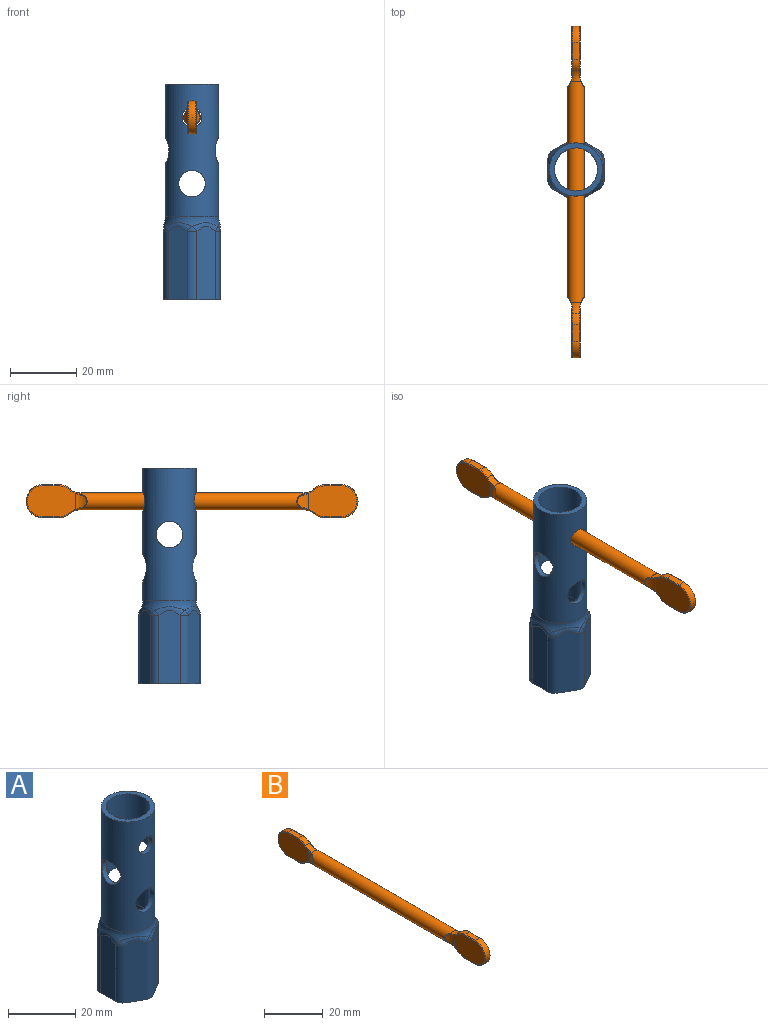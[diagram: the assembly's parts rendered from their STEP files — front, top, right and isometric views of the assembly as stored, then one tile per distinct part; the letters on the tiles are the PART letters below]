
ASSEMBLY  parts=2 mates=1
PART A: 60 faces, bbox 20.5x20.5x65 mm
  f0: cylinder r=8mm len=40mm, axis (0,0,-1), area 1745mm2, adj f9,f10,f54,f55,f56,f57,f58,f59
  f1: cylinder r=6.5mm len=40mm, axis (0,0,-1), area 1363.3mm2, adj f10,f35,f54,f55,f56,f57,f58,f59
  f2: plane 22.22x5.5mm, normal (0.5,0.87,0), area 137mm2, adj f8,f11,f16,f20
  f3: plane 22.22x5.5mm, normal (-0.5,0.87,0), area 137mm2, adj f8,f11,f12,f24
  f4: plane 22.22x6.35mm, normal (-1,0,0), area 137mm2, adj f8,f12,f13,f28
  f5: plane 22.22x5.5mm, normal (-0.5,-0.87,0), area 137mm2, adj f8,f13,f14,f25
  f6: plane 22.22x5.5mm, normal (0.5,-0.87,0), area 137mm2, adj f8,f14,f15,f21
  f7: plane 22.22x6.35mm, normal (1,0,0), area 137mm2, adj f8,f15,f16,f17
  f8: plane 18.7x17mm, normal (0,0,-1), area 78.4mm2, adj f2,f3,f4,f5,f6,f7,f11,f12
  f9: torus R=13mm, axis (0,0,1), area 112.2mm2, adj f0,f17,f20,f21,f24,f25,f28
  f10: plane 16x16mm, normal (0,0,1), area 68.3mm2, adj f0,f1
  f11: cylinder r=3mm len=20.55mm, axis (0,0,-1), area 64.6mm2, adj f2,f3,f8,f22
  f12: cylinder r=3mm len=20.55mm, axis (0,0,-1), area 64.6mm2, adj f3,f4,f8,f26
  f13: cylinder r=3mm len=20.55mm, axis (0,0,-1), area 64.6mm2, adj f4,f5,f8,f27
  f14: cylinder r=3mm len=20.55mm, axis (0,0,-1), area 64.6mm2, adj f5,f6,f8,f23
  f15: cylinder r=3mm len=20.55mm, axis (0,0,-1), area 64.6mm2, adj f6,f7,f8,f19
  f16: cylinder r=3mm len=20.55mm, axis (0,0,-1), area 64.6mm2, adj f2,f7,f8,f18
  f17: bspline ~10.91x3.77mm, area 12.7mm2, adj f7,f9,f18,f19
  f18: sphere r=3mm, area 2.9mm2, adj f16,f17,f20
  f19: sphere r=3mm, area 2.9mm2, adj f15,f17,f21
  f20: bspline ~9.65x6.03mm, area 12.7mm2, adj f2,f9,f18,f22
  f21: bspline ~9.49x6.34mm, area 12.7mm2, adj f6,f9,f19,f23
  f22: sphere r=3mm, area 2.9mm2, adj f11,f20,f24
  f23: sphere r=3mm, area 2.9mm2, adj f14,f21,f25
  f24: bspline ~9.49x6.34mm, area 12.7mm2, adj f3,f9,f22,f26
  f25: bspline ~9.65x6.03mm, area 12.7mm2, adj f5,f9,f23,f27
  f26: sphere r=3mm, area 2.9mm2, adj f12,f24,f28
  f27: sphere r=3mm, area 2.9mm2, adj f13,f25,f28
  f28: bspline ~10.91x3.77mm, area 12.7mm2, adj f4,f9,f26,f27
  f29: plane 22.22x5.5mm, normal (-0.5,-0.87,0), area 137mm2, adj f8,f36,f41,f45
  f30: plane 22.22x5.5mm, normal (0.5,-0.87,0), area 137mm2, adj f8,f36,f37,f49
  f31: plane 22.22x6.35mm, normal (1,0,0), area 137mm2, adj f8,f37,f38,f53
  f32: plane 22.22x5.5mm, normal (0.5,0.87,0), area 137mm2, adj f8,f38,f39,f50
  f33: plane 22.22x5.5mm, normal (-0.5,0.87,0), area 137mm2, adj f8,f39,f40,f46
  f34: plane 22.22x6.35mm, normal (-1,0,0), area 137mm2, adj f8,f40,f41,f42
  f35: torus R=13mm, axis (0,0,1), area 120mm2, adj f1,f42,f45,f46,f49,f50,f53
  f36: cylinder r=1.5mm len=20.55mm, axis (0,0,-1), area 32.3mm2, adj f8,f29,f30,f47
  f37: cylinder r=1.5mm len=20.55mm, axis (0,0,-1), area 32.3mm2, adj f8,f30,f31,f51
  f38: cylinder r=1.5mm len=20.55mm, axis (0,0,-1), area 32.3mm2, adj f8,f31,f32,f52
  f39: cylinder r=1.5mm len=20.55mm, axis (0,0,-1), area 32.3mm2, adj f8,f32,f33,f48
  f40: cylinder r=1.5mm len=20.55mm, axis (0,0,-1), area 32.3mm2, adj f8,f33,f34,f44
  f41: cylinder r=1.5mm len=20.55mm, axis (0,0,-1), area 32.3mm2, adj f8,f29,f34,f43
  f42: bspline ~9.54x3.25mm, area 6.1mm2, adj f34,f35,f43,f44
  f43: sphere r=1.5mm, area 0.7mm2, adj f41,f42,f45
  f44: sphere r=1.5mm, area 0.7mm2, adj f40,f42,f46
  f45: bspline ~8.37x5.06mm, area 6.1mm2, adj f29,f35,f43,f47
  f46: bspline ~8.29x5.22mm, area 6.1mm2, adj f33,f35,f44,f48
  f47: sphere r=1.5mm, area 0.7mm2, adj f36,f45,f49
  f48: sphere r=1.5mm, area 0.7mm2, adj f39,f46,f50
  f49: bspline ~8.29x5.22mm, area 6.1mm2, adj f30,f35,f47,f51
  f50: bspline ~8.37x5.06mm, area 6.1mm2, adj f32,f35,f48,f52
  f51: sphere r=1.5mm, area 0.7mm2, adj f37,f49,f53
  f52: sphere r=1.5mm, area 0.7mm2, adj f38,f50,f53
  f53: bspline ~9.54x3.25mm, area 6.1mm2, adj f31,f35,f51,f52
  f54: cylinder r=4mm len=8mm, axis (0,-1,0), area 41.2mm2, adj f0,f1
  f55: cylinder r=4mm len=8mm, axis (0,-1,0), area 41.3mm2, adj f0,f1
  f56: cylinder r=3mm len=6mm, axis (0,-1,0), area 29.6mm2, adj f0,f1
  f57: cylinder r=3mm len=6mm, axis (0,-1,0), area 29.6mm2, adj f0,f1
  f58: cylinder r=4mm len=8mm, axis (-1,0,0), area 41.3mm2, adj f0,f1
  f59: cylinder r=4mm len=8mm, axis (-1,0,0), area 41.3mm2, adj f0,f1
PART B: 63 faces, bbox 10x100.6x10.6 mm
  f0: cylinder r=5mm len=5mm, axis (0,1,0), area 10.6mm2, adj f1,f3,f14,f23
  f1: sphere r=5mm, area 7.7mm2, adj f0,f7,f16,f25
  f2: torus R=7.5mm, axis (0,1,0), area 8.5mm2, adj f5,f6,f17,f19,f28,f30
  f3: sphere r=5mm, area 33.1mm2, adj f0,f4,f12,f22
  f4: cylinder r=5mm len=5mm, axis (0,1,0), area 10.6mm2, adj f3,f5,f13,f24
  f5: sphere r=5mm, area 7.7mm2, adj f2,f4,f15,f26
  f6: cylinder r=2.5mm len=66.77mm, axis (0,1,0), area 1023.8mm2, adj f2,f7,f21,f31,f34,f38,f52,f62
  f7: torus R=7.5mm, axis (0,1,0), area 8.5mm2, adj f1,f6,f18,f20,f27,f29
  f8: cylinder r=5mm len=4.59mm, axis (0,0,1), area 12mm2, adj f9,f29,f30,f31
  f9: plane 14.65x9.29mm, normal (1,0,0), area 117.4mm2, adj f8,f22,f23,f24,f25,f26,f27,f28
  f10: cylinder r=5mm len=4.59mm, axis (0,0,1), area 12mm2, adj f11,f19,f20,f21
  f11: plane 14.65x9.29mm, normal (-1,0,0), area 117.4mm2, adj f10,f12,f13,f14,f15,f16,f17,f18
  f12: torus R=4.64mm, axis (1,0,0), area 5.1mm2, adj f3,f11,f13,f14
  f13: cylinder r=0.25mm len=5mm, axis (0,1,0), area 1.7mm2, adj f4,f11,f12,f15
  f14: cylinder r=0.25mm len=5mm, axis (0,1,0), area 1.7mm2, adj f0,f11,f12,f16
  f15: torus R=4.64mm, axis (1,0,0), area 1.2mm2, adj f5,f11,f13,f17
  f16: torus R=4.64mm, axis (1,0,0), area 1.2mm2, adj f1,f11,f14,f18
  f17: bspline ~3.79x2.46mm, area 0.7mm2, adj f2,f11,f15,f19
  f18: bspline ~3.79x2.46mm, area 0.7mm2, adj f7,f11,f16,f20
  f19: bspline ~3.06x1.17mm, area 0.5mm2, adj f2,f10,f17,f21
  f20: bspline ~2.79x1.11mm, area 0.5mm2, adj f7,f10,f18,f21
  f21: bspline ~4.33x2.31mm, area 1.3mm2, adj f6,f10,f19,f20
  f22: torus R=4.64mm, axis (-1,0,0), area 5.1mm2, adj f3,f9,f23,f24
  f23: cylinder r=0.25mm len=5mm, axis (0,1,0), area 1.7mm2, adj f0,f9,f22,f25
  f24: cylinder r=0.25mm len=5mm, axis (0,1,0), area 1.7mm2, adj f4,f9,f22,f26
  f25: torus R=4.64mm, axis (-1,0,0), area 1.2mm2, adj f1,f9,f23,f27
  f26: torus R=4.64mm, axis (-1,0,0), area 1.2mm2, adj f5,f9,f24,f28
  f27: bspline ~3.79x2.46mm, area 0.7mm2, adj f7,f9,f25,f29
  f28: bspline ~3.79x2.46mm, area 0.7mm2, adj f2,f9,f26,f30
  f29: bspline ~3.06x1.17mm, area 0.5mm2, adj f7,f8,f27,f31
  f30: bspline ~2.79x1.11mm, area 0.5mm2, adj f2,f8,f28,f31
  f31: bspline ~4.33x2.31mm, area 1.3mm2, adj f6,f8,f29,f30
  f32: cylinder r=5mm len=5mm, axis (0,-1,0), area 10.6mm2, adj f33,f35,f45,f54
  f33: sphere r=5mm, area 7.7mm2, adj f32,f38,f47,f56
  f34: torus R=7.5mm, axis (0,-1,0), area 8.5mm2, adj f6,f37,f48,f50,f59,f61
  f35: sphere r=5mm, area 33.1mm2, adj f32,f36,f43,f53
  f36: cylinder r=5mm len=5mm, axis (0,-1,0), area 10.6mm2, adj f35,f37,f44,f55
  f37: sphere r=5mm, area 7.7mm2, adj f34,f36,f46,f57
  f38: torus R=7.5mm, axis (0,-1,0), area 8.5mm2, adj f6,f33,f49,f51,f58,f60
  f39: cylinder r=5mm len=4.59mm, axis (0,0,1), area 12mm2, adj f40,f60,f61,f62
  f40: plane 14.65x9.29mm, normal (1,0,0), area 117.4mm2, adj f39,f53,f54,f55,f56,f57,f58,f59
  f41: cylinder r=5mm len=4.59mm, axis (0,0,1), area 12mm2, adj f42,f50,f51,f52
  f42: plane 14.65x9.29mm, normal (-1,0,0), area 117.4mm2, adj f41,f43,f44,f45,f46,f47,f48,f49
  f43: torus R=4.64mm, axis (1,0,0), area 5.1mm2, adj f35,f42,f44,f45
  f44: cylinder r=0.25mm len=5mm, axis (0,-1,0), area 1.7mm2, adj f36,f42,f43,f46
  f45: cylinder r=0.25mm len=5mm, axis (0,-1,0), area 1.7mm2, adj f32,f42,f43,f47
  f46: torus R=4.64mm, axis (1,0,0), area 1.2mm2, adj f37,f42,f44,f48
  f47: torus R=4.64mm, axis (1,0,0), area 1.2mm2, adj f33,f42,f45,f49
  f48: bspline ~3.79x2.46mm, area 0.7mm2, adj f34,f42,f46,f50
  f49: bspline ~3.79x2.46mm, area 0.7mm2, adj f38,f42,f47,f51
  f50: bspline ~3.06x1.17mm, area 0.5mm2, adj f34,f41,f48,f52
  f51: bspline ~2.79x1.11mm, area 0.5mm2, adj f38,f41,f49,f52
  f52: bspline ~4.33x2.31mm, area 1.3mm2, adj f6,f41,f50,f51
  f53: torus R=4.64mm, axis (-1,0,0), area 5.1mm2, adj f35,f40,f54,f55
  f54: cylinder r=0.25mm len=5mm, axis (0,-1,0), area 1.7mm2, adj f32,f40,f53,f56
  f55: cylinder r=0.25mm len=5mm, axis (0,-1,0), area 1.7mm2, adj f36,f40,f53,f57
  f56: torus R=4.64mm, axis (-1,0,0), area 1.2mm2, adj f33,f40,f54,f58
  f57: torus R=4.64mm, axis (-1,0,0), area 1.2mm2, adj f37,f40,f55,f59
  f58: bspline ~3.79x2.46mm, area 0.7mm2, adj f38,f40,f56,f60
  f59: bspline ~3.79x2.46mm, area 0.7mm2, adj f34,f40,f57,f61
  f60: bspline ~3.06x1.17mm, area 0.5mm2, adj f38,f39,f58,f62
  f61: bspline ~2.79x1.11mm, area 0.5mm2, adj f34,f39,f59,f62
  f62: bspline ~4.33x2.31mm, area 1.3mm2, adj f6,f39,f60,f61
PLACE A at identity fixed
PLACE B t=(0,-6.77,55)mm
MATE slider B.f0 <-> A.f56  axis (0,1,0) through (0,-6.77,55)mm
